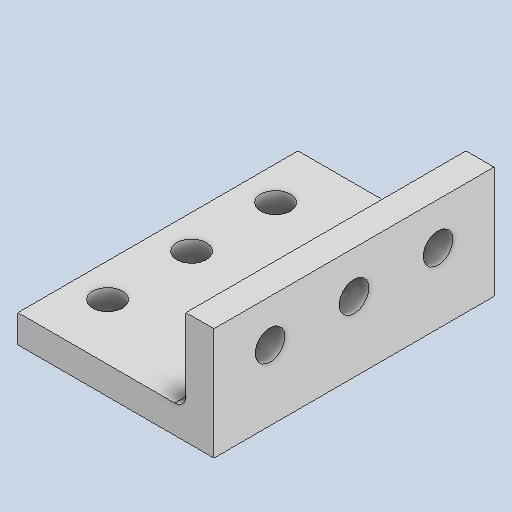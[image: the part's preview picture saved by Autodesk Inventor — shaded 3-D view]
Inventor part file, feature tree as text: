
AUTODESK INVENTOR PART (.ipt)
format: ipt  version: 2022 (Build 260153000, 153)  size: 145,408 bytes
history: native  units: in
note: dims shown in document units (in); Inventor stores cm internally (conversion verified against a paired STEP export)
features: extrude x3, sketch x3, other x3, reference x2, fillet x1
ambient origin geometry x8: Origin, YZ Plane, XZ Plane, XY Plane, X Axis, Y Axis, Z Axis, Center Point
bodies: Solid1 (feature_tree)
feature tree (12):
  extrude  "Extrusion1"  Depth=0.0039in
  extrude  "Extrusion2"  Depth=1.378in
  extrude  "Extrusion3"  Depth=1.9685in TaperAngle=0.0deg
  fillet  "Fillet1"  Radius=0.2087in
  sketch  "Sketch1"  dims[d0=0.0039in d1=0.0039in]
  reference  "Reference1"
  reference  "Reference2"
  sketch  "Sketch2"  dims[d2=0.1969in d3=1.378in]
  sketch  "Sketch3"  dims[d4=0.7874in d5=1.9685in d6=0.0in d7=0.2087in d8=0.3937in d9=0.2087in d10=0.0in d11=0.0in d12=0.2087in d13=0.3937in d14=0.2362in d15=0.2087in d16=0.0in d17=0.0in d18=0.0787in]
  other  "Linear Rail Assembly.iam"
  other  "endcap insert:1"
  other  "backboard_MIR:1"
